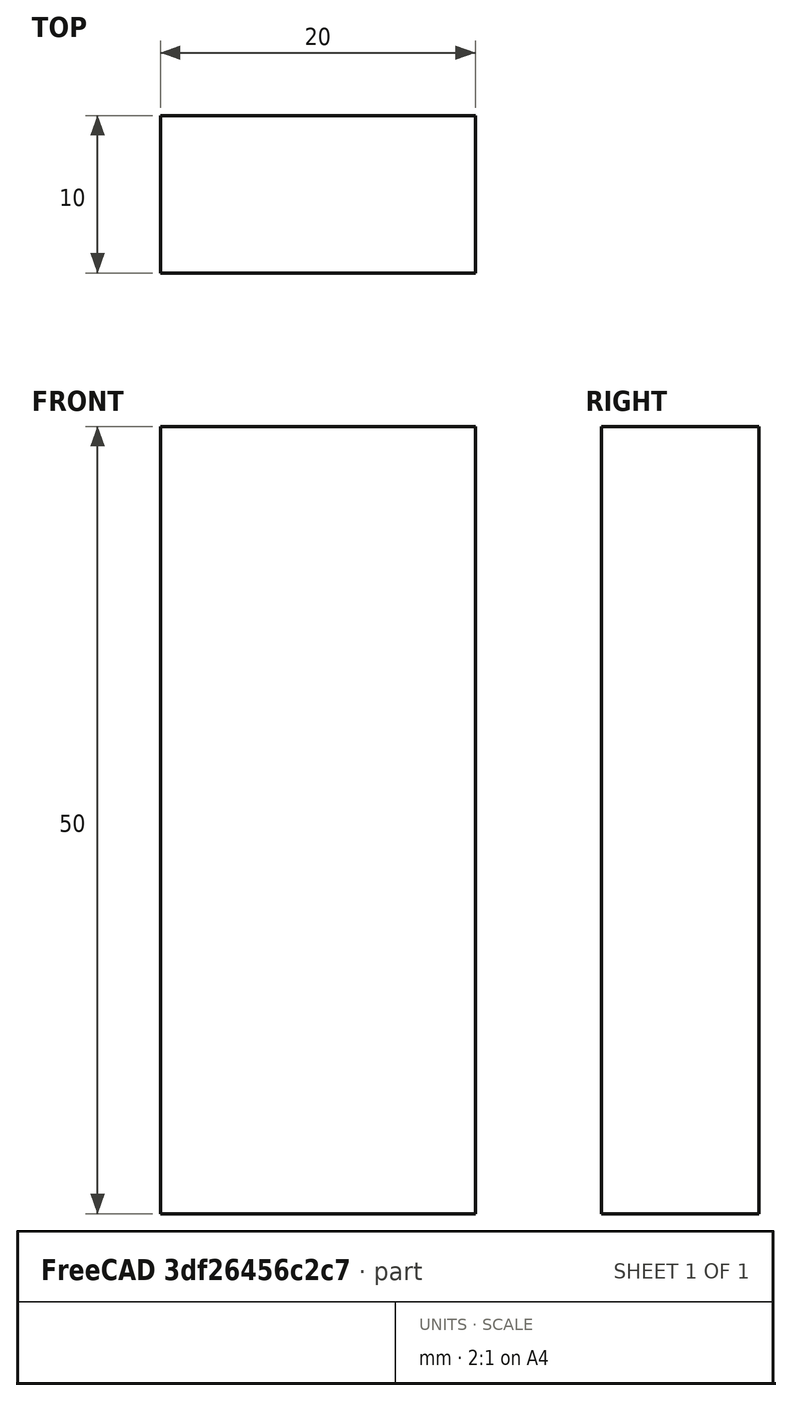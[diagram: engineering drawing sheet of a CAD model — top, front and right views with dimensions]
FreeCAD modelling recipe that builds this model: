
FCSTD DOCUMENT  (FreeCAD 0.15R4671 (Git))
Label: Flat Bar 20x10 EN10058 S235JR
License: All rights reserved
LicenseURL: http://en.wikipedia.org/wiki/All_rights_reserved
objects: Sketcher::SketchObject×1, Part::Extrusion×1
note: 2 computed .brp shape members not serialized (recipe doc carries the construction recipe); baked Part::Feature solids carry a one-line shape summary decoded from their .brp

FEATURE [Sketcher::SketchObject] Sketch
  sketch-geometry (4):
    g0: LineSegment StartX=-10 StartY=-5 StartZ=0 EndX=10 EndY=-5 EndZ=0
    g1: LineSegment StartX=10 StartY=-5 StartZ=0 EndX=10 EndY=5 EndZ=0
    g2: LineSegment StartX=10 StartY=5 StartZ=0 EndX=-10 EndY=5 EndZ=0
    g3: LineSegment StartX=-10 StartY=5 StartZ=0 EndX=-10 EndY=-5 EndZ=0
  constraints (12):
    c: Coincident(g0,g1)
    c: Coincident(g1,g2)
    c: Coincident(g2,g3)
    c: Coincident(g3,g0)
    c: Horizontal(g0)
    c: Horizontal(g2)
    c: Vertical(g1)
    c: Vertical(g3)
    c: Symmetric(g1,g2,g-2)
    c: Symmetric(g0,g1,g-1)
    c: DistanceY(g1) = 10
    c: DistanceX(g0) = 20
FEATURE [Part::Extrusion] Extrude  label="Flat Bar 20x10 EN10058 S235JR"
  Base = -> Sketch
  Dir = (0,0,50)
  Solid = true
